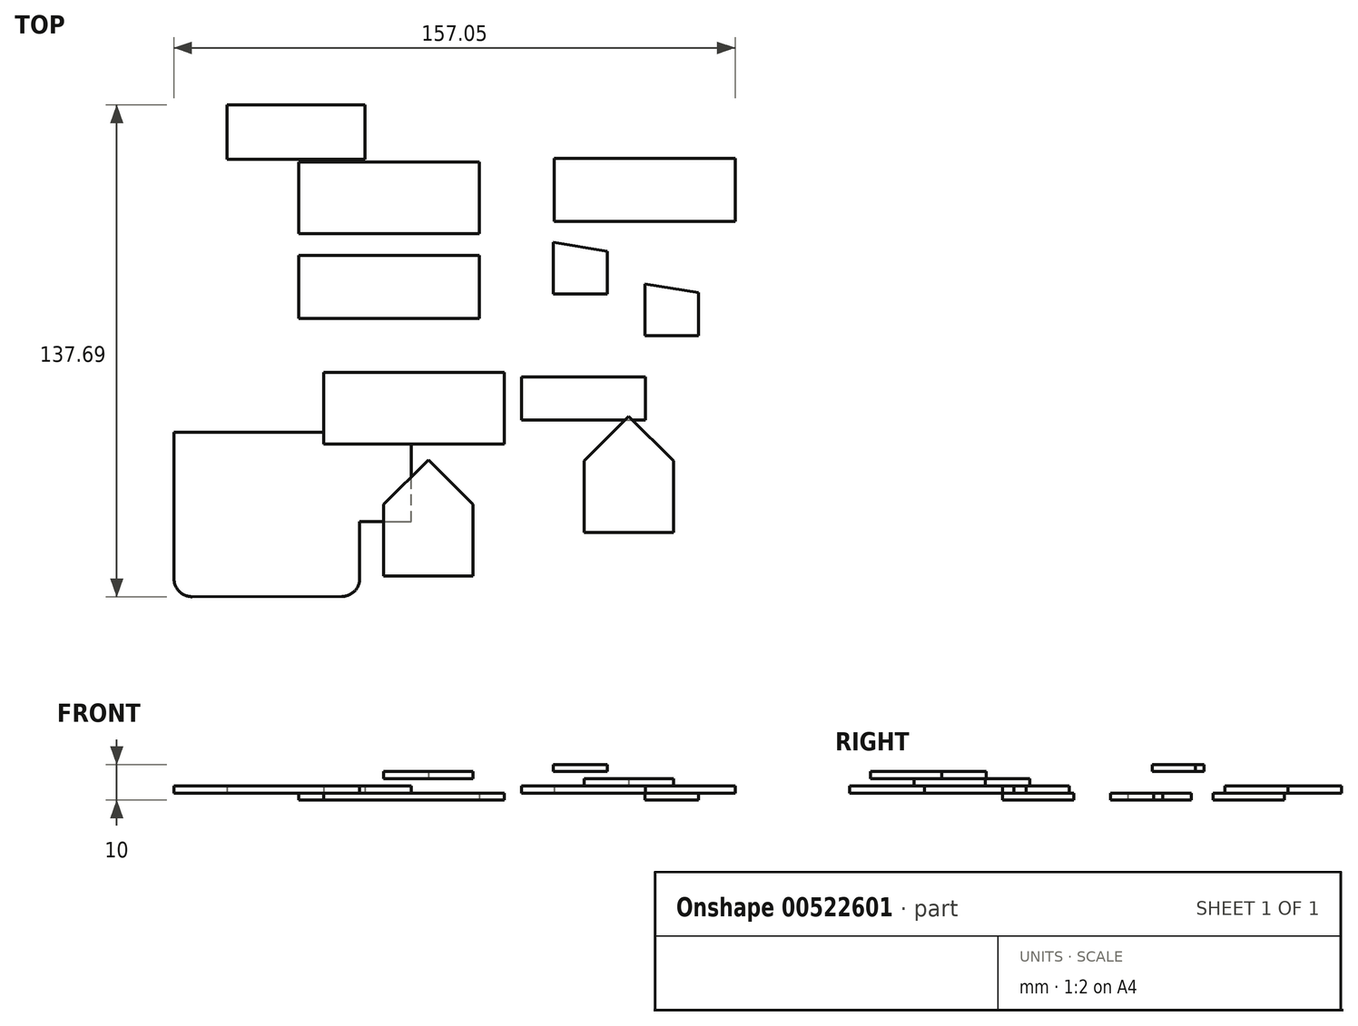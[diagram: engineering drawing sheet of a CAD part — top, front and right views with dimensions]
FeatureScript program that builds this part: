
annotation { "Feature Type Name" : "Feature", "Feature Type Description" : "" }
export const myFeature = defineFeature(function(context is Context, id is Id, definition is map)
    precondition{}
    {
        {
            var Q0;
            Q0=qCreatedBy(makeId("Top.planeOp"),FACE);
            var sketch = newSketch(context, id + "F0", { "sketchPlane" : qUnion([Q0])});
            skLineSegment(sketch, "E0.bottom", {"start": v(-43.56, -5.44) * mm, "end": v(7.03, -5.44) * mm});
            skLineSegment(sketch, "E0.top", {"start": v(-43.56, -25.44) * mm, "end": v(7.03, -25.44) * mm});
            skLineSegment(sketch, "E0.left", {"start": v(-43.56, -5.44) * mm, "end": v(-43.56, -25.44) * mm});
            skLineSegment(sketch, "E0.right", {"start": v(7.03, -5.44) * mm, "end": v(7.03, -25.44) * mm});
            skSolve(sketch);
        }
        {
            var Q0;
            Q0=makeQuery(id+"F0.imprint","IMPRINT",FACE,{"disambiguationData":[TD([[makeQuery(id+"F0.imprint","IMPRINT",EDGE,{"derivedFrom":sQuery(id+"F0.wireOp",EDGE,"E0.bottom")}),-1.0]])]});
            extrude(context, id + "F1", {"entities" : qUnion([Q0]), "depth" : 2 * mm, "offsetDistance" : 25 * mm});
        }
        {
            var Q0;
            Q0=qCreatedBy(makeId("Top.planeOp"),FACE);
            var sketch = newSketch(context, id + "F2", { "sketchPlane" : qUnion([Q0])});
            skLineSegment(sketch, "E1.bottom", {"start": v(-50.53, 53.5) * mm, "end": v(0, 53.5) * mm});
            skLineSegment(sketch, "E1.top", {"start": v(-50.53, 33.5) * mm, "end": v(0, 33.5) * mm});
            skLineSegment(sketch, "E1.left", {"start": v(-50.53, 53.5) * mm, "end": v(-50.53, 33.5) * mm});
            skLineSegment(sketch, "E1.right", {"start": v(0, 53.5) * mm, "end": v(0, 33.5) * mm});
            skSolve(sketch);
        }
        {
            var Q0;
            Q0=makeQuery(id+"F2.imprint","IMPRINT",FACE,{"disambiguationData":[TD([[makeQuery(id+"F2.imprint","IMPRINT",EDGE,{"derivedFrom":sQuery(id+"F2.wireOp",EDGE,"E1.bottom")}),-1.0]])]});
            extrude(context, id + "F3", {"entities" : qUnion([Q0]), "depth" : 2 * mm, "offsetDistance" : 25 * mm});
        }
        {
            var Q0;
            Q0=qCreatedBy(makeId("Top.planeOp"),FACE);
            var sketch = newSketch(context, id + "F4", { "sketchPlane" : qUnion([Q0])});
            skLineSegment(sketch, "E2.bottom", {"start": v(-50.6, 27.38) * mm, "end": v(0, 27.38) * mm});
            skLineSegment(sketch, "E2.top", {"start": v(-50.6, 9.7) * mm, "end": v(0, 9.7) * mm});
            skLineSegment(sketch, "E2.left", {"start": v(-50.6, 27.38) * mm, "end": v(-50.6, 9.7) * mm});
            skLineSegment(sketch, "E2.right", {"start": v(0, 27.38) * mm, "end": v(0, 9.7) * mm});
            skSolve(sketch);
        }
        {
            var Q0;
            Q0 = qSketchRegion(id + "F4", true);
            extrude(context, id + "F5", {"entities" : qUnion([Q0]), "depth" : 2 * mm, "offsetDistance" : 25 * mm});
        }
        {
            var Q0;
            Q0=makeQuery(id+"F5.opExtrude","CAP_FACE",FACE,{"disambiguationData":[OSD([sQuery(id+"F4.wireOp",EDGE,"E2.bottom"),sQuery(id+"F4.wireOp",EDGE,"E2.top"),sQuery(id+"F4.wireOp",EDGE,"E2.left"),sQuery(id+"F4.wireOp",EDGE,"E2.right")])],"isStart":false});
            var sketch = newSketch(context, id + "F6", { "sketchPlane" : qUnion([Q0])});
            skLineSegment(sketch, "E3.bottom", {"start": v(21, 54.5) * mm, "end": v(71.6, 54.5) * mm});
            skLineSegment(sketch, "E3.top", {"start": v(21, 36.81) * mm, "end": v(71.6, 36.81) * mm});
            skLineSegment(sketch, "E3.left", {"start": v(21, 54.5) * mm, "end": v(21, 36.81) * mm});
            skLineSegment(sketch, "E3.right", {"start": v(71.6, 54.5) * mm, "end": v(71.6, 36.81) * mm});
            skSolve(sketch);
        }
        {
            var Q0;
            Q0 = qSketchRegion(id + "F6", true);
            extrude(context, id + "F7", {"entities" : qUnion([Q0]), "depth" : 2 * mm, "offsetDistance" : 25 * mm});
        }
        {
            var Q0;
            Q0=makeQuery(id+"F7.opExtrude","CAP_FACE",FACE,{"disambiguationData":[OSD([sQuery(id+"F6.wireOp",EDGE,"E3.bottom"),sQuery(id+"F6.wireOp",EDGE,"E3.top"),sQuery(id+"F6.wireOp",EDGE,"E3.left"),sQuery(id+"F6.wireOp",EDGE,"E3.right")])],"isStart":false});
            var sketch = newSketch(context, id + "F8", { "sketchPlane" : qUnion([Q0])});
            skLineSegment(sketch, "E4", {"start": v(29.35, -30.22) * mm, "end": v(29.35, -50.22) * mm});
            skLineSegment(sketch, "E5", {"start": v(29.35, -50.22) * mm, "end": v(50.57, -50.22) * mm});
            skLineSegment(sketch, "E6.MirrorCS", {"start": v(54.35, -30.22) * mm, "end": v(54.35, -50.22) * mm});
            skLineSegment(sketch, "E7.MirrorCS", {"start": v(54.35, -50.22) * mm, "end": v(33.13, -50.22) * mm});
            skLineSegment(sketch, "E8", {"start": v(29.35, -30.22) * mm, "end": v(41.85, -17.72) * mm});
            skLineSegment(sketch, "E9", {"start": v(41.85, -17.72) * mm, "end": v(54.35, -30.22) * mm});
            skSolve(sketch);
        }
        {
            var Q0;
            Q0=makeQuery(id+"F8.imprint","IMPRINT",FACE,{"disambiguationData":[TD([[makeQuery(id+"F8.imprint","IMPRINT",EDGE,{"derivedFrom":sQuery(id+"F8.wireOp",EDGE,"E4")}),1.0]])]});
            extrude(context, id + "F9", {"entities" : qUnion([Q0]), "depth" : 2 * mm, "offsetDistance" : 25 * mm});
        }
        {
            var Q0;
            Q0=makeQuery(id+"F9.opExtrude","CAP_FACE",FACE,{"disambiguationData":[OSD([sQuery(id+"F8.wireOp",EDGE,"E4"),sQuery(id+"F8.wireOp",EDGE,"E5"),sQuery(id+"F8.wireOp",EDGE,"E6.MirrorCS"),sQuery(id+"F8.wireOp",EDGE,"E7.MirrorCS"),sQuery(id+"F8.wireOp",EDGE,"E8"),sQuery(id+"F8.wireOp",EDGE,"E9")])],"isStart":false});
            var sketch = newSketch(context, id + "F10", { "sketchPlane" : qUnion([Q0])});
            skLineSegment(sketch, "E10", {"start": v(-26.75, -42.41) * mm, "end": v(-26.75, -62.41) * mm});
            skLineSegment(sketch, "E11.MirrorCS", {"start": v(-1.75, -42.41) * mm, "end": v(-1.75, -62.41) * mm});
            skLineSegment(sketch, "E12", {"start": v(-26.75, -42.41) * mm, "end": v(-14.25, -29.91) * mm});
            skLineSegment(sketch, "E13", {"start": v(-14.25, -29.91) * mm, "end": v(-1.75, -42.41) * mm});
            skLineSegment(sketch, "E14", {"start": v(-26.75, -62.41) * mm, "end": v(-1.75, -62.41) * mm});
            skSolve(sketch);
        }
        {
            var Q0;
            Q0=makeQuery(id+"F10.imprint","IMPRINT",FACE,{"disambiguationData":[TD([[makeQuery(id+"F10.imprint","IMPRINT",EDGE,{"derivedFrom":sQuery(id+"F10.wireOp",EDGE,"E10")}),1.0]])]});
            extrude(context, id + "F11", {"entities" : qUnion([Q0]), "depth" : 2 * mm, "offsetDistance" : 25 * mm});
        }
        {
            var Q0;
            Q0=makeQuery(id+"F11.opExtrude","CAP_FACE",FACE,{"disambiguationData":[OSD([sQuery(id+"F10.wireOp",EDGE,"E10"),sQuery(id+"F10.wireOp",EDGE,"E11.MirrorCS"),sQuery(id+"F10.wireOp",EDGE,"E12"),sQuery(id+"F10.wireOp",EDGE,"E13"),sQuery(id+"F10.wireOp",EDGE,"E14")])],"isStart":false});
            var sketch = newSketch(context, id + "F12", { "sketchPlane" : qUnion([Q0])});
            skLineSegment(sketch, "E15", {"start": v(20.77, 16.53) * mm, "end": v(20.77, 28.53) * mm});
            skLineSegment(sketch, "E16", {"start": v(35.77, 28.53) * mm, "end": v(35.77, 16.53) * mm});
            skLineSegment(sketch, "E17", {"start": v(35.77, 16.53) * mm, "end": v(20.77, 16.53) * mm});
            skLineSegment(sketch, "E18", {"start": v(20.77, 28.53) * mm, "end": v(20.77, 31.03) * mm});
            skLineSegment(sketch, "E19", {"start": v(20.77, 31.03) * mm, "end": v(35.77, 28.53) * mm});
            skSolve(sketch);
        }
        {
            var Q0;
            Q0=makeQuery(id+"F12.imprint","IMPRINT",FACE,{"disambiguationData":[TD([[makeQuery(id+"F12.imprint","IMPRINT",EDGE,{"derivedFrom":sQuery(id+"F12.wireOp",EDGE,"E15")}),-1.0]])]});
            extrude(context, id + "F13", {"entities" : qUnion([Q0]), "depth" : 2 * mm, "offsetDistance" : 25 * mm});
        }
        {
            var Q0;
            Q0=qCreatedBy(makeId("Top.planeOp"),FACE);
            var sketch = newSketch(context, id + "F14", { "sketchPlane" : qUnion([Q0])});
            skLineSegment(sketch, "E20", {"start": v(46.35, 4.88) * mm, "end": v(46.35, 16.88) * mm});
            skLineSegment(sketch, "E21", {"start": v(61.35, 16.88) * mm, "end": v(61.35, 4.88) * mm});
            skLineSegment(sketch, "E22", {"start": v(61.35, 4.88) * mm, "end": v(46.35, 4.88) * mm});
            skLineSegment(sketch, "E23", {"start": v(46.35, 16.88) * mm, "end": v(46.35, 19.38) * mm});
            skLineSegment(sketch, "E24", {"start": v(46.35, 19.38) * mm, "end": v(61.35, 16.88) * mm});
            skSolve(sketch);
        }
        {
            var Q0;
            Q0=makeQuery(id+"F14.imprint","IMPRINT",FACE,{"disambiguationData":[TD([[makeQuery(id+"F14.imprint","IMPRINT",EDGE,{"derivedFrom":sQuery(id+"F14.wireOp",EDGE,"E20")}),-1.0]])]});
            extrude(context, id + "F15", {"entities" : qUnion([Q0]), "depth" : 2 * mm, "offsetDistance" : 25 * mm});
        }
        {
            var Q0;
            Q0=makeQuery(id+"F15.opExtrude","CAP_FACE",FACE,{"disambiguationData":[OSD([sQuery(id+"F14.wireOp",EDGE,"E20"),sQuery(id+"F14.wireOp",EDGE,"E21"),sQuery(id+"F14.wireOp",EDGE,"E22"),sQuery(id+"F14.wireOp",EDGE,"E23"),sQuery(id+"F14.wireOp",EDGE,"E24")])],"isStart":false});
            var sketch = newSketch(context, id + "F16", { "sketchPlane" : qUnion([Q0])});
            skLineSegment(sketch, "E25.bottom", {"start": v(-70.61, 69.45) * mm, "end": v(-32, 69.45) * mm});
            skLineSegment(sketch, "E25.top", {"start": v(-70.61, 54.24) * mm, "end": v(-32, 54.24) * mm});
            skLineSegment(sketch, "E25.left", {"start": v(-70.61, 69.45) * mm, "end": v(-70.61, 54.24) * mm});
            skLineSegment(sketch, "E25.right", {"start": v(-32, 69.45) * mm, "end": v(-32, 54.24) * mm});
            skSolve(sketch);
        }
        {
            var Q0;
            Q0 = qSketchRegion(id + "F16", true);
            extrude(context, id + "F17", {"entities" : qUnion([Q0]), "depth" : 2 * mm, "offsetDistance" : 25 * mm});
        }
        {
            var Q0;
            Q0=makeQuery(id+"F1.opExtrude","CAP_FACE",FACE,{"disambiguationData":[OSD([sQuery(id+"F0.wireOp",EDGE,"E0.bottom"),sQuery(id+"F0.wireOp",EDGE,"E0.top"),sQuery(id+"F0.wireOp",EDGE,"E0.left"),sQuery(id+"F0.wireOp",EDGE,"E0.right")])],"isStart":false});
            var sketch = newSketch(context, id + "F18", { "sketchPlane" : qUnion([Q0])});
            skLineSegment(sketch, "E26", {"start": v(-33.48, -62.22) * mm, "end": v(-33.48, -47.22) * mm});
            skLineSegment(sketch, "E27", {"start": v(-33.48, -47.22) * mm, "end": v(-18.98, -47.22) * mm});
            skLineSegment(sketch, "E28", {"start": v(-18.98, -47.22) * mm, "end": v(-18.98, -22.22) * mm});
            skLineSegment(sketch, "E29", {"start": v(-18.98, -22.22) * mm, "end": v(-85.45, -22.22) * mm});
            skLineSegment(sketch, "E30", {"start": v(-85.45, -22.22) * mm, "end": v(-85.45, -47.22) * mm});
            skLineSegment(sketch, "E31", {"start": v(-85.45, -47.22) * mm, "end": v(-85.45, -63.24) * mm});
            skLineSegment(sketch, "E32", {"start": v(-33.48, -62.22) * mm, "end": v(-33.48, -63.15) * mm});
            skLineSegment(sketch, "E33", {"start": v(-80.44, -68.24) * mm, "end": v(-38.47, -68.18) * mm});
            skPoint(sketch, "E34.visualSharp", {"position": v(-85.45, -68.25) * mm});
            skArc(sketch, "E34.filletArc", {"start": v(-85.45, -63.24) * mm, "mid": v(-83.98, -66.78) * mm, "end": v(-80.44, -68.24) * mm});
            skPoint(sketch, "E35.visualSharp", {"position": v(-33.44, -68.18) * mm});
            skArc(sketch, "E35.filletArc", {"start": v(-38.47, -68.18) * mm, "mid": v(-34.93, -66.7) * mm, "end": v(-33.48, -63.15) * mm});
            skSolve(sketch);
        }
        {
            var Q0;
            Q0=makeQuery(id+"F18.imprint","IMPRINT",FACE,{"disambiguationData":[TD([[makeQuery(id+"F18.imprint","IMPRINT",EDGE,{"derivedFrom":sQuery(id+"F18.wireOp",EDGE,"E26")}),1.0]])]});
            extrude(context, id + "F19", {"entities" : qUnion([Q0]), "depth" : 2 * mm, "offsetDistance" : 25 * mm});
        }
        {
            var Q0;
            Q0=makeQuery(id+"F1.opExtrude","CAP_FACE",FACE,{"disambiguationData":[OSD([sQuery(id+"F0.wireOp",EDGE,"E0.bottom"),sQuery(id+"F0.wireOp",EDGE,"E0.top"),sQuery(id+"F0.wireOp",EDGE,"E0.left"),sQuery(id+"F0.wireOp",EDGE,"E0.right")])],"isStart":false});
            var sketch = newSketch(context, id + "F20", { "sketchPlane" : qUnion([Q0])});
            skLineSegment(sketch, "E36.bottom", {"start": v(11.84, -6.74) * mm, "end": v(46.45, -6.74) * mm});
            skLineSegment(sketch, "E36.top", {"start": v(11.84, -18.74) * mm, "end": v(46.45, -18.74) * mm});
            skLineSegment(sketch, "E36.left", {"start": v(11.84, -6.74) * mm, "end": v(11.84, -18.74) * mm});
            skLineSegment(sketch, "E36.right", {"start": v(46.45, -6.74) * mm, "end": v(46.45, -18.74) * mm});
            skSolve(sketch);
        }
        {
            var Q0;
            Q0 = qSketchRegion(id + "F20", true);
            extrude(context, id + "F21", {"entities" : qUnion([Q0]), "operationType" : NewBodyOperationType.ADD, "depth" : 2 * mm, "offsetDistance" : 25 * mm});
        }
    });
